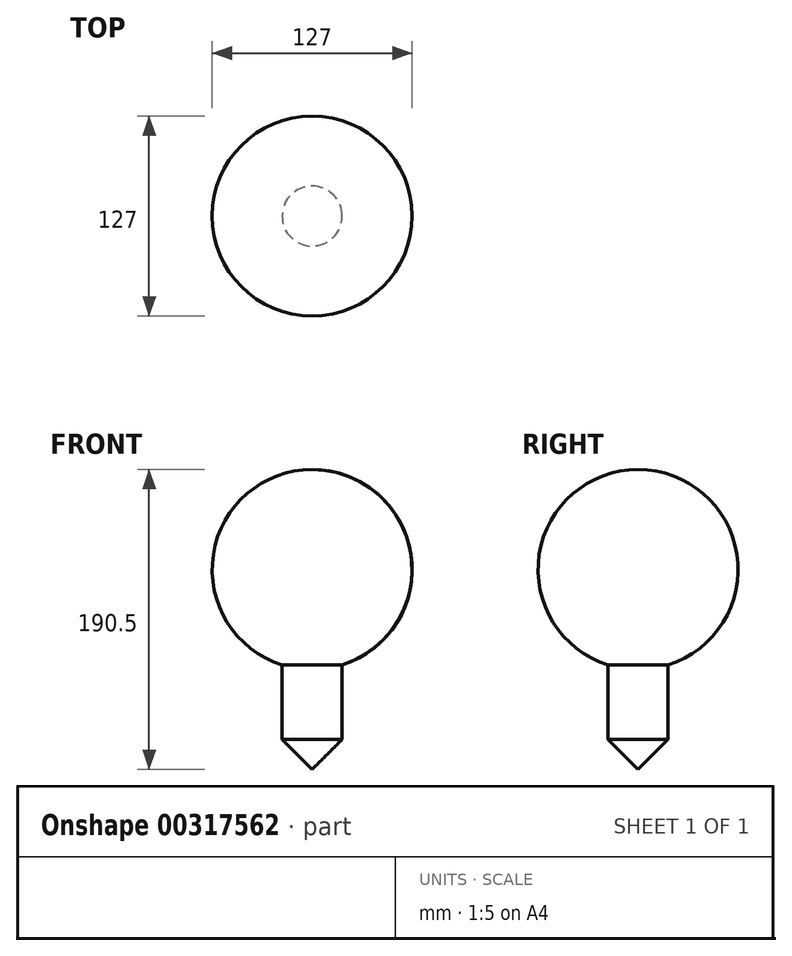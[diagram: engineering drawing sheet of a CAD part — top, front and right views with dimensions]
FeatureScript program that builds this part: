
annotation { "Feature Type Name" : "Feature", "Feature Type Description" : "" }
export const myFeature = defineFeature(function(context is Context, id is Id, definition is map)
    precondition{}
    {
        {
            var Q0;
            Q0=qCreatedBy(makeId("Front.planeOp"),FACE);
            var sketch = newSketch(context, id + "F0", { "sketchPlane" : qUnion([Q0])});
            skArc(sketch, "E0", {"start": v(0, 63.5) * mm, "mid": v(-63.5, 0) * mm, "end": v(0, -63.5) * mm});
            skLineSegment(sketch, "E1", {"start": v(0, 0) * mm, "end": v(0, 63.5) * mm});
            skLineSegment(sketch, "E2", {"start": v(0, 0) * mm, "end": v(0, -63.5) * mm});
            skSolve(sketch);
        }
        {
            var Q0;
            Q0=makeQuery(id+"F0.imprint","IMPRINT",FACE,{"disambiguationData":[TD([[makeQuery(id+"F0.imprint","IMPRINT",EDGE,{"derivedFrom":sQuery(id+"F0.wireOp",EDGE,"E0")}),1.0]])]});
            var Q1;
            Q1=sQuery(id+"F0.wireOp",EDGE,"E1");
            revolve(context, id + "F1", {"entities" : qUnion([Q0]), "axis" : qUnion([Q1]), "revolveType" : RevolveType.FULL});
        }
        {
            var Q0;
            Q0=qCreatedBy(makeId("Top.planeOp"),FACE);
            var sketch = newSketch(context, id + "F2", { "sketchPlane" : qUnion([Q0])});
            skCircle(sketch, "E3", {"center": v(0, 0) * mm, "radius": 19.05 * mm});
            skSolve(sketch);
        }
        {
            var Q0;
            Q0 = qSketchRegion(id + "F2", true);
            extrude(context, id + "F3", {"entities" : qUnion([Q0]), "operationType" : NewBodyOperationType.ADD, "oppositeDirection" : true, "depth" : 127 * mm});
        }
        {
            var Q0;
            Q0=makeQuery(id+"F3.opExtrude","CAP_EDGE",EDGE,{"disambiguationData":[OSD([sQuery(id+"F2.wireOp",EDGE,"E3")])],"isStart":false});
            chamfer(context, id + "F4", {"entities" : qUnion([Q0]), "width" : 19.05 * mm, "tangentPropagation" : true});
        }
    });
